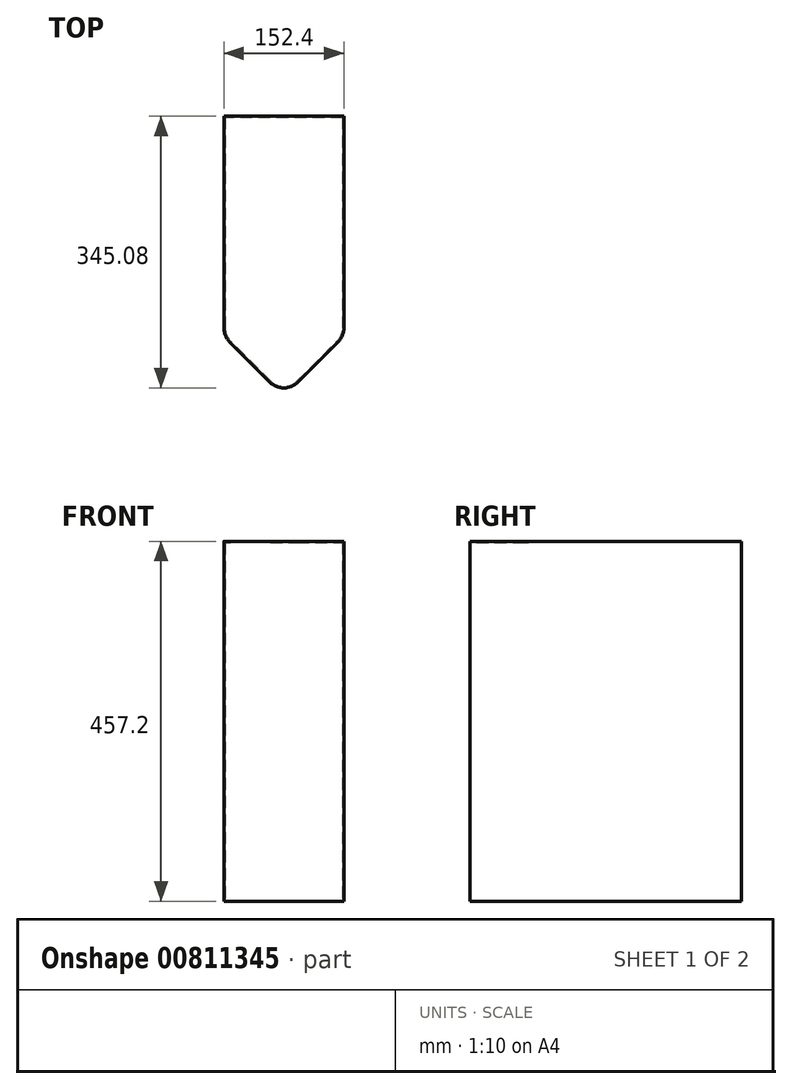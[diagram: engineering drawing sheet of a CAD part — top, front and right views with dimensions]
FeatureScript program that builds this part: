
annotation { "Feature Type Name" : "Feature", "Feature Type Description" : "" }
export const myFeature = defineFeature(function(context is Context, id is Id, definition is map)
    precondition{}
    {
        {
            var Q0;
            Q0=qCreatedBy(makeId("Top.planeOp"),FACE);
            var sketch = newSketch(context, id + "F0", { "sketchPlane" : qUnion([Q0])});
            skLineSegment(sketch, "E0.bottom", {"start": v(76.2, 177.8) * mm, "end": v(-76.2, 177.8) * mm});
            skLineSegment(sketch, "E0.top", {"start": v(76.2, -177.8) * mm, "end": v(-76.2, -177.8) * mm, "construction": true});
            skLineSegment(sketch, "E0.left", {"start": v(76.2, 177.8) * mm, "end": v(76.2, -177.8) * mm});
            skLineSegment(sketch, "E0.right", {"start": v(-76.2, 177.8) * mm, "end": v(-76.2, -177.8) * mm});
            skPoint(sketch, "E0.middle", {"position": v(0, 0) * mm});
            skLineSegment(sketch, "E1", {"start": v(0, -177.8) * mm, "end": v(76.2, -101.6) * mm});
            skLineSegment(sketch, "E2", {"start": v(0, -177.8) * mm, "end": v(-76.2, -101.6) * mm});
            skSolve(sketch);
        }
        {
            var Q0;
            Q0 = qSketchRegion(id + "F0", true);
            extrude(context, id + "F1", {"entities" : qUnion([Q0]), "depth" : 457.2 * mm, "offsetDistance" : 25.4 * mm});
        }
        {
            var Q0;
            Q0=makeQuery(id+"F1.opExtrude","SWEPT_EDGE",EDGE,{"disambiguationData":[OSD([sQuery(id+"F0.wireOp",EDGE,"E1"),sQuery(id+"F0.wireOp",EDGE,"E2")])]});
            var Q1;
            Q1=makeQuery(id+"F1.opExtrude","SWEPT_EDGE",EDGE,{"disambiguationData":[OSD([sQuery(id+"F0.wireOp",EDGE,"E0.left"),sQuery(id+"F0.wireOp",EDGE,"E1")])]});
            var Q2;
            Q2=makeQuery(id+"F1.opExtrude","SWEPT_EDGE",EDGE,{"disambiguationData":[OSD([sQuery(id+"F0.wireOp",EDGE,"E0.right"),sQuery(id+"F0.wireOp",EDGE,"E2")])]});
            fillet(context, id + "F2", {"entities" : qUnion([Q0, Q1, Q2]), "radius" : 25.4 * mm, "tangentPropagation" : true, "allowEdgeOverflow" : false});
        }
        {
            var Q0;
            Q0=makeQuery(id+"F1.opExtrude","CAP_FACE",FACE,{"disambiguationData":[OSD([sQuery(id+"F0.wireOp",EDGE,"E0.bottom"),sQuery(id+"F0.wireOp",EDGE,"E0.left"),sQuery(id+"F0.wireOp",EDGE,"E0.right"),sQuery(id+"F0.wireOp",EDGE,"E1"),sQuery(id+"F0.wireOp",EDGE,"E2")])],"isStart":true});
            shell(context, id + "F3", {"entities" : qUnion([Q0]), "thickness" : 1.59 * mm});
        }
    });
